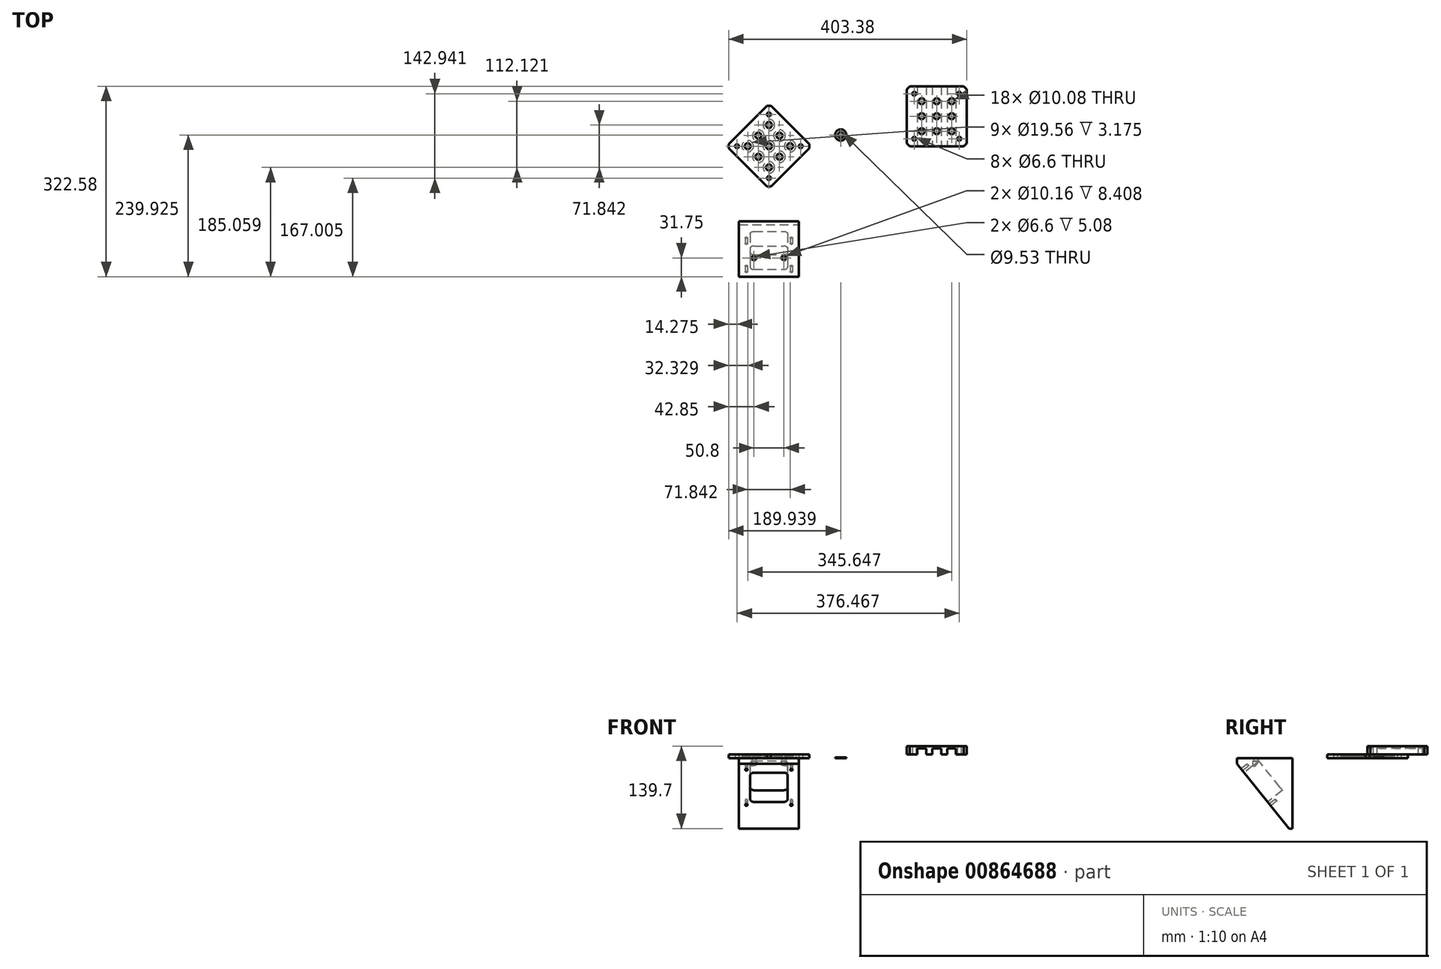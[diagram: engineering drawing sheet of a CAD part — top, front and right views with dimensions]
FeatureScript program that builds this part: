
annotation { "Feature Type Name" : "Feature", "Feature Type Description" : "" }
export const myFeature = defineFeature(function(context is Context, id is Id, definition is map)
    precondition{}
    {
        {
            var Q0;
            Q0=qCreatedBy(makeId("Top.planeOp"),FACE);
            var sketch = newSketch(context, id + "F0", { "sketchPlane" : qUnion([Q0])});
            skCircle(sketch, "E0", {"center": v(0, 0) * mm, "radius": 53.97 * mm, "construction": true});
            skPoint(sketch, "E1", {"position": v(0, 53.97) * mm});
            skPoint(sketch, "E2", {"position": v(53.97, 0) * mm});
            skPoint(sketch, "E3", {"position": v(0, -53.97) * mm});
            skPoint(sketch, "E4", {"position": v(-53.97, 0) * mm});
            skLineSegment(sketch, "E5", {"start": v(0, -71.84) * mm, "end": v(-71.84, 0) * mm});
            skLineSegment(sketch, "E6", {"start": v(-71.84, 0) * mm, "end": v(0, 71.84) * mm});
            skLineSegment(sketch, "E7", {"start": v(0, 71.84) * mm, "end": v(71.84, 0) * mm});
            skLineSegment(sketch, "E8", {"start": v(71.84, 0) * mm, "end": v(0, -71.84) * mm});
            skSolve(sketch);
        }
        {
            var Q0;
            Q0 = qSketchRegion(id + "F0", true);
            extrude(context, id + "F1", {"entities" : qUnion([Q0]), "depth" : 6.35 * mm, "offsetDistance" : 25.4 * mm});
        }
        {
            var Q0;
            Q0=sQuery(id+"F0.wireOp",VERTEX,"E3");
            var Q1;
            Q1=sQuery(id+"F0.wireOp",VERTEX,"E4");
            var Q2;
            Q2=sQuery(id+"F0.wireOp",VERTEX,"E2");
            var Q3;
            Q3=sQuery(id+"F0.wireOp",VERTEX,"E1");
            var Q4;
            Q4=makeQuery(id+"F1.opExtrude","SWEPT_BODY",BODY,{"disambiguationData":[OSD([sQuery(id+"F0.wireOp",EDGE,"E5"),sQuery(id+"F0.wireOp",EDGE,"E6"),sQuery(id+"F0.wireOp",EDGE,"E7"),sQuery(id+"F0.wireOp",EDGE,"E8")])]});
            hole(context, id + "F2", {"style" : HoleStyle.SIMPLE, "endStyle" : HoleEndStyle.THROUGH, "oppositeDirection" : true, "holeDiameter" : 6.6 * mm, "majorDiameter" : 6.35 * mm, "isTappedThrough" : true, "tappedDepth" : 12.7 * mm, "tapClearance" : 3, "locations" : qUnion([Q0, Q1, Q2, Q3]), "scope" : qUnion([Q4])});
        }
        {
            var Q0;
            Q0=makeQuery(id+"F0.imprint","IMPRINT",FACE,{"disambiguationData":[TD([[makeQuery(id+"F0.imprint","IMPRINT",EDGE,{"derivedFrom":sQuery(id+"F0.wireOp",EDGE,"E5")}),-1.0]])]});
            var sketch = newSketch(context, id + "F3", { "sketchPlane" : qUnion([Q0])});
            skPoint(sketch, "E9", {"position": v(0, 0) * mm});
            skPoint(sketch, "E10", {"position": v(-17.96, 17.96) * mm});
            skPoint(sketch, "E11", {"position": v(17.96, -17.96) * mm});
            skPoint(sketch, "E12", {"position": v(-35.92, 0) * mm});
            skPoint(sketch, "E13", {"position": v(-17.96, -17.96) * mm});
            skPoint(sketch, "E14", {"position": v(0, -35.92) * mm});
            skPoint(sketch, "E15", {"position": v(35.92, 0) * mm});
            skPoint(sketch, "E16", {"position": v(17.96, 17.96) * mm});
            skPoint(sketch, "E17", {"position": v(0, 35.92) * mm});
            skLineSegment(sketch, "E18", {"start": v(0, 0) * mm, "end": v(0, -88) * mm});
            skLineSegment(sketch, "E19", {"start": v(0, 0) * mm, "end": v(-58.21, -58.21) * mm});
            skLineSegment(sketch, "E20", {"start": v(-17.96, -17.96) * mm, "end": v(-35.92, 0) * mm});
            skLineSegment(sketch, "E21", {"start": v(-35.92, 0) * mm, "end": v(0, 35.92) * mm});
            skLineSegment(sketch, "E22", {"start": v(0, 35.92) * mm, "end": v(35.92, 0) * mm});
            skLineSegment(sketch, "E23", {"start": v(35.92, 0) * mm, "end": v(0, -35.92) * mm});
            skLineSegment(sketch, "E24", {"start": v(0, -35.92) * mm, "end": v(-17.96, -17.96) * mm});
            skSolve(sketch);
        }
        {
            var Q0;
            Q0=sQuery(id+"F3.wireOp",VERTEX,"E14");
            var Q1;
            Q1=sQuery(id+"F3.wireOp",VERTEX,"E13");
            var Q2;
            Q2=sQuery(id+"F3.wireOp",VERTEX,"E12");
            var Q3;
            Q3=sQuery(id+"F3.wireOp",VERTEX,"E10");
            var Q4;
            Q4=sQuery(id+"F3.wireOp",VERTEX,"E17");
            var Q5;
            Q5=sQuery(id+"F3.wireOp",VERTEX,"E16");
            var Q6;
            Q6=sQuery(id+"F3.wireOp",VERTEX,"E15");
            var Q7;
            Q7=sQuery(id+"F3.wireOp",VERTEX,"E11");
            var Q8;
            Q8=sQuery(id+"F3.wireOp",VERTEX,"E9");
            var Q9;
            Q9=makeQuery(id+"F1.opExtrude","SWEPT_BODY",BODY,{"disambiguationData":[OSD([sQuery(id+"F0.wireOp",EDGE,"E5"),sQuery(id+"F0.wireOp",EDGE,"E6"),sQuery(id+"F0.wireOp",EDGE,"E7"),sQuery(id+"F0.wireOp",EDGE,"E8")])]});
            hole(context, id + "F4", {"style" : HoleStyle.C_BORE, "endStyle" : HoleEndStyle.THROUGH, "oppositeDirection" : true, "holeDiameter" : 10.08 * mm, "cBoreDiameter" : 19.56 * mm, "cBoreDepth" : 3.17 * mm, "majorDiameter" : 6.35 * mm, "isTappedThrough" : true, "tappedDepth" : 12.7 * mm, "tapClearance" : 3, "locations" : qUnion([Q0, Q1, Q2, Q3, Q4, Q5, Q6, Q7, Q8]), "scope" : qUnion([Q9])});
        }
        {
            var Q0;
            Q0=makeQuery(id+"F1.opExtrude","SWEPT_EDGE",EDGE,{"disambiguationData":[OSD([sQuery(id+"F0.wireOp",EDGE,"E5"),sQuery(id+"F0.wireOp",EDGE,"E6")])]});
            var Q1;
            Q1=makeQuery(id+"F1.opExtrude","SWEPT_EDGE",EDGE,{"disambiguationData":[OSD([sQuery(id+"F0.wireOp",EDGE,"E6"),sQuery(id+"F0.wireOp",EDGE,"E7")])]});
            var Q2;
            Q2=makeQuery(id+"F1.opExtrude","SWEPT_EDGE",EDGE,{"disambiguationData":[OSD([sQuery(id+"F0.wireOp",EDGE,"E7"),sQuery(id+"F0.wireOp",EDGE,"E8")])]});
            var Q3;
            Q3=makeQuery(id+"F1.opExtrude","SWEPT_EDGE",EDGE,{"disambiguationData":[OSD([sQuery(id+"F0.wireOp",EDGE,"E5"),sQuery(id+"F0.wireOp",EDGE,"E8")])]});
            chamfer(context, id + "F5", {"entities" : qUnion([Q0, Q1, Q2, Q3]), "width" : 5.08 * mm, "tangentPropagation" : true});
        }
        {
            var Q0;
            Q0=makeQuery(id+"F1.opExtrude","CAP_FACE",FACE,{"disambiguationData":[OSD([sQuery(id+"F0.wireOp",EDGE,"E5"),sQuery(id+"F0.wireOp",EDGE,"E6"),sQuery(id+"F0.wireOp",EDGE,"E7"),sQuery(id+"F0.wireOp",EDGE,"E8")])],"isStart":false});
            var sketch = newSketch(context, id + "F6", { "sketchPlane" : qUnion([Q0])});
            skLineSegment(sketch, "E25.bottom", {"start": v(335.13, 0) * mm, "end": v(233.53, 0) * mm});
            skLineSegment(sketch, "E25.top", {"start": v(335.13, 101.6) * mm, "end": v(233.53, 101.6) * mm});
            skLineSegment(sketch, "E25.left", {"start": v(335.13, 0) * mm, "end": v(335.13, 101.6) * mm});
            skLineSegment(sketch, "E25.right", {"start": v(233.53, 0) * mm, "end": v(233.53, 101.6) * mm});
            skSolve(sketch);
        }
        {
            var Q0;
            Q0 = qSketchRegion(id + "F6", true);
            extrude(context, id + "F7", {"entities" : qUnion([Q0]), "depth" : 13.97 * mm, "offsetDistance" : 25.4 * mm});
        }
        {
            var Q0;
            Q0=makeQuery(id+"F7.opExtrude","CAP_FACE",FACE,{"disambiguationData":[OSD([sQuery(id+"F6.wireOp",EDGE,"E25.bottom"),sQuery(id+"F6.wireOp",EDGE,"E25.top"),sQuery(id+"F6.wireOp",EDGE,"E25.left"),sQuery(id+"F6.wireOp",EDGE,"E25.right")])],"isStart":true});
            var sketch = newSketch(context, id + "F8", { "sketchPlane" : qUnion([Q0])});
            skCircle(sketch, "E26", {"center": v(284.33, -50.8) * mm, "radius": 53.98 * mm});
            skPoint(sketch, "E27", {"position": v(322.5, -88.97) * mm});
            skPoint(sketch, "E28", {"position": v(322.5, -12.63) * mm});
            skPoint(sketch, "E29", {"position": v(246.16, -12.63) * mm});
            skPoint(sketch, "E30", {"position": v(246.16, -88.97) * mm});
            skLineSegment(sketch, "E31", {"start": v(284.33, -50.8) * mm, "end": v(246.16, -88.97) * mm});
            skLineSegment(sketch, "E32", {"start": v(284.33, -50.8) * mm, "end": v(246.16, -12.63) * mm});
            skLineSegment(sketch, "E33", {"start": v(284.33, -50.8) * mm, "end": v(322.5, -12.63) * mm});
            skLineSegment(sketch, "E34", {"start": v(284.33, -50.8) * mm, "end": v(322.5, -88.97) * mm});
            skSolve(sketch);
        }
        {
            var Q0;
            Q0=sQuery(id+"F8.wireOp",VERTEX,"E31.end");
            var Q1;
            Q1=sQuery(id+"F8.wireOp",VERTEX,"E29");
            var Q2;
            Q2=sQuery(id+"F8.wireOp",VERTEX,"E28");
            var Q3;
            Q3=sQuery(id+"F8.wireOp",VERTEX,"E27");
            var Q4;
            Q4=makeQuery(id+"F7.opExtrude","SWEPT_BODY",BODY,{"disambiguationData":[OSD([sQuery(id+"F6.wireOp",EDGE,"E25.bottom"),sQuery(id+"F6.wireOp",EDGE,"E25.top"),sQuery(id+"F6.wireOp",EDGE,"E25.left"),sQuery(id+"F6.wireOp",EDGE,"E25.right")])]});
            hole(context, id + "F9", {"style" : HoleStyle.SIMPLE, "endStyle" : HoleEndStyle.THROUGH, "holeDiameter" : 6.6 * mm, "majorDiameter" : 6.35 * mm, "isTappedThrough" : true, "tappedDepth" : 12.7 * mm, "tapClearance" : 3, "locations" : qUnion([Q0, Q1, Q2, Q3]), "scope" : qUnion([Q4])});
        }
        {
            var Q0;
            Q0=makeQuery(id+"F7.opExtrude","SWEPT_FACE",FACE,{"disambiguationData":[OSD([sQuery(id+"F6.wireOp",EDGE,"E25.bottom")])]});
            var sketch = newSketch(context, id + "F10", { "sketchPlane" : qUnion([Q0])});
            skLineSegment(sketch, "E35.bottom", {"start": v(317.1, 6.35) * mm, "end": v(302.36, 6.35) * mm});
            skLineSegment(sketch, "E35.top", {"start": v(317.1, 16.51) * mm, "end": v(302.36, 16.51) * mm});
            skLineSegment(sketch, "E35.left", {"start": v(317.1, 6.35) * mm, "end": v(317.1, 16.51) * mm});
            skLineSegment(sketch, "E35.right", {"start": v(302.36, 6.35) * mm, "end": v(302.36, 16.5) * mm});
            skLineSegment(sketch, "E36.bottom", {"start": v(291.7, 6.35) * mm, "end": v(276.96, 6.35) * mm});
            skLineSegment(sketch, "E36.top", {"start": v(291.7, 16.51) * mm, "end": v(276.96, 16.51) * mm});
            skLineSegment(sketch, "E36.left", {"start": v(291.7, 6.35) * mm, "end": v(291.7, 16.51) * mm});
            skLineSegment(sketch, "E36.right", {"start": v(276.96, 6.35) * mm, "end": v(276.96, 16.51) * mm});
            skLineSegment(sketch, "E37.bottom", {"start": v(266.3, 6.35) * mm, "end": v(251.56, 6.35) * mm});
            skLineSegment(sketch, "E37.top", {"start": v(266.3, 16.51) * mm, "end": v(251.56, 16.51) * mm});
            skLineSegment(sketch, "E37.left", {"start": v(266.3, 6.35) * mm, "end": v(266.3, 16.51) * mm});
            skLineSegment(sketch, "E37.right", {"start": v(251.56, 6.35) * mm, "end": v(251.56, 16.5) * mm});
            skSolve(sketch);
        }
        {
            var Q0;
            Q0 = qSketchRegion(id + "F10", true);
            extrude(context, id + "F11", {"entities" : qUnion([Q0]), "operationType" : NewBodyOperationType.REMOVE, "endBound" : BoundingType.THROUGH_ALL, "oppositeDirection" : true, "depth" : 25.4 * mm, "offsetDistance" : 25.4 * mm});
        }
        {
            var Q0;
            Q0=makeQuery(id+"F7.opExtrude","SWEPT_EDGE",EDGE,{"disambiguationData":[OSD([sQuery(id+"F6.wireOp",EDGE,"E25.bottom"),sQuery(id+"F6.wireOp",EDGE,"E25.left")])]});
            var Q1;
            Q1=makeQuery(id+"F7.opExtrude","SWEPT_EDGE",EDGE,{"disambiguationData":[OSD([sQuery(id+"F6.wireOp",EDGE,"E25.bottom"),sQuery(id+"F6.wireOp",EDGE,"E25.right")])]});
            var Q2;
            Q2=makeQuery(id+"F7.opExtrude","SWEPT_EDGE",EDGE,{"disambiguationData":[OSD([sQuery(id+"F6.wireOp",EDGE,"E25.top"),sQuery(id+"F6.wireOp",EDGE,"E25.right")])]});
            var Q3;
            Q3=makeQuery(id+"F7.opExtrude","SWEPT_EDGE",EDGE,{"disambiguationData":[OSD([sQuery(id+"F6.wireOp",EDGE,"E25.top"),sQuery(id+"F6.wireOp",EDGE,"E25.left")])]});
            chamfer(context, id + "F12", {"entities" : qUnion([Q0, Q1, Q2, Q3]), "width" : 5.08 * mm, "tangentPropagation" : true});
        }
        {
            var Q0;
            Q0=qCreatedBy(makeId("Top.planeOp"),FACE);
            var sketch = newSketch(context, id + "F13", { "sketchPlane" : qUnion([Q0])});
            skCircle(sketch, "E38", {"center": v(121.69, 18.95) * mm, "radius": 4.76 * mm});
            skCircle(sketch, "E39", {"center": v(121.69, 18.95) * mm, "radius": 9.53 * mm});
            skSolve(sketch);
        }
        {
            var Q0;
            Q0 = qSketchRegion(id + "F13", true);
            extrude(context, id + "F14", {"entities" : qUnion([Q0]), "depth" : 1.02 * mm, "offsetDistance" : 25.4 * mm});
        }
        {
            var Q0;
            Q0=qCreatedBy(makeId("Right.planeOp"),FACE);
            var sketch = newSketch(context, id + "F15", { "sketchPlane" : qUnion([Q0])});
            skLineSegment(sketch, "E40", {"start": v(-228.6, 0) * mm, "end": v(-127, -127) * mm});
            skLineSegment(sketch, "E41", {"start": v(-127, -127) * mm, "end": v(-127, 0) * mm});
            skLineSegment(sketch, "E42", {"start": v(-127, 0) * mm, "end": v(-228.6, 0) * mm});
            skSolve(sketch);
        }
        {
            var Q0;
            Q0 = qSketchRegion(id + "F15", true);
            extrude(context, id + "F16", {"entities" : qUnion([Q0]), "endBound" : BoundingType.SYMMETRIC, "depth" : 101.6 * mm, "offsetDistance" : 25.4 * mm});
        }
        {
            var Q0;
            Q0=makeQuery(id+"F16.opExtrude","SWEPT_FACE",FACE,{"disambiguationData":[OSD([sQuery(id+"F15.wireOp",EDGE,"E40")])]});
            var sketch = newSketch(context, id + "F17", { "sketchPlane" : qUnion([Q0])});
            skCircle(sketch, "E43", {"center": v(0, 79.3) * mm, "radius": 53.98 * mm});
            skLineSegment(sketch, "E44", {"start": v(0, 79.3) * mm, "end": v(-38.17, 41.14) * mm});
            skLineSegment(sketch, "E45", {"start": v(0, 79.3) * mm, "end": v(38.17, 117.47) * mm});
            skLineSegment(sketch, "E46", {"start": v(0, 79.3) * mm, "end": v(38.17, 41.14) * mm});
            skLineSegment(sketch, "E47", {"start": v(0, 79.3) * mm, "end": v(-38.17, 117.47) * mm});
            skLineSegment(sketch, "E48", {"start": v(0, 79.3) * mm, "end": v(0, 25.33) * mm});
            skSolve(sketch);
        }
        {
            var Q0;
            Q0=sQuery(id+"F17.wireOp",VERTEX,"E46.end");
            var Q1;
            Q1=sQuery(id+"F17.wireOp",VERTEX,"E44.end");
            var Q2;
            Q2=sQuery(id+"F17.wireOp",VERTEX,"E47.end");
            var Q3;
            Q3=sQuery(id+"F17.wireOp",VERTEX,"E45.end");
            var Q4;
            Q4=makeQuery(id+"F16.opExtrude","SWEPT_BODY",BODY,{"disambiguationData":[OSD([sQuery(id+"F15.wireOp",EDGE,"E40"),sQuery(id+"F15.wireOp",EDGE,"E41"),sQuery(id+"F15.wireOp",EDGE,"E42")])]});
            hole(context, id + "F18", {"style" : HoleStyle.SIMPLE, "endStyle" : HoleEndStyle.BLIND, "holeDiameter" : 3.97 * mm, "majorDiameter" : 6.35 * mm, "holeDepth" : 12.7 * mm, "isTappedThrough" : true, "tappedDepth" : 12.7 * mm, "tapClearance" : 3, "locations" : qUnion([Q0, Q1, Q2, Q3]), "scope" : qUnion([Q4])});
        }
        {
            var Q0;
            Q0=makeQuery(id+"F16.opExtrude","CAP_FACE",FACE,{"disambiguationData":[OSD([sQuery(id+"F15.wireOp",EDGE,"E40"),sQuery(id+"F15.wireOp",EDGE,"E41"),sQuery(id+"F15.wireOp",EDGE,"E42")])],"isStart":false});
            var sketch = newSketch(context, id + "F19", { "sketchPlane" : qUnion([Q0])});
            skLineSegment(sketch, "E49", {"start": v(-220.98, -9.52) * mm, "end": v(-220.98, 0) * mm});
            skLineSegment(sketch, "E50", {"start": v(-220.98, 0) * mm, "end": v(-228.6, 0) * mm});
            skLineSegment(sketch, "E51", {"start": v(-228.6, 0) * mm, "end": v(-220.98, -9.52) * mm});
            skLineSegment(sketch, "E52", {"start": v(-127, -127) * mm, "end": v(-127, -119.38) * mm});
            skLineSegment(sketch, "E53", {"start": v(-127, -119.38) * mm, "end": v(-133.1, -119.38) * mm});
            skLineSegment(sketch, "E54", {"start": v(-133.1, -119.38) * mm, "end": v(-127, -127) * mm});
            skSolve(sketch);
        }
        {
            var Q0;
            Q0=makeQuery(id+"F19.imprint","IMPRINT",FACE,{"disambiguationData":[TD([[makeQuery(id+"F19.imprint","IMPRINT",EDGE,{"derivedFrom":sQuery(id+"F19.wireOp",EDGE,"E49")}),1.0]])]});
            var Q1;
            Q1=makeQuery(id+"F19.imprint","IMPRINT",FACE,{"disambiguationData":[TD([[makeQuery(id+"F19.imprint","IMPRINT",EDGE,{"derivedFrom":sQuery(id+"F19.wireOp",EDGE,"E52")}),1.0]])]});
            extrude(context, id + "F20", {"entities" : qUnion([Q0, Q1]), "operationType" : NewBodyOperationType.REMOVE, "endBound" : BoundingType.THROUGH_ALL, "oppositeDirection" : true, "depth" : 25.4 * mm, "offsetDistance" : 25.4 * mm});
        }
        {
            var Q0;
            Q0=makeQuery(id+"F20.boolean.opBoolean","COPY",FACE,{"derivedFrom":makeQuery(id+"F20.opExtrude","SWEPT_FACE",FACE,{"disambiguationData":[OSD([sQuery(id+"F19.wireOp",EDGE,"E53")])]})});
            var sketch = newSketch(context, id + "F21", { "sketchPlane" : qUnion([Q0])});
            skPoint(sketch, "E55", {"position": v(-25.4, 189.23) * mm});
            skPoint(sketch, "E56", {"position": v(25.4, 189.23) * mm});
            skSolve(sketch);
        }
        {
            var Q0;
            Q0=sQuery(id+"F21.wireOp",VERTEX,"E55");
            var Q1;
            Q1=sQuery(id+"F21.wireOp",VERTEX,"E56");
            var Q2;
            Q2=makeQuery(id+"F16.opExtrude","SWEPT_BODY",BODY,{"disambiguationData":[OSD([sQuery(id+"F15.wireOp",EDGE,"E40"),sQuery(id+"F15.wireOp",EDGE,"E41"),sQuery(id+"F15.wireOp",EDGE,"E42")])]});
            hole(context, id + "F22", {"style" : HoleStyle.C_BORE, "endStyle" : HoleEndStyle.THROUGH, "holeDiameter" : 6.6 * mm, "cBoreDiameter" : 10.16 * mm, "cBoreDepth" : 114.3 * mm, "majorDiameter" : 6.35 * mm, "isTappedThrough" : true, "tappedDepth" : 12.7 * mm, "tapClearance" : 3, "startFromSketch" : true, "locations" : qUnion([Q0, Q1]), "scope" : qUnion([Q2])});
        }
        {
            var Q0;
            Q0=makeQuery(id+"F16.opExtrude","SWEPT_FACE",FACE,{"disambiguationData":[OSD([sQuery(id+"F15.wireOp",EDGE,"E40")])]});
            var sketch = newSketch(context, id + "F23", { "sketchPlane" : qUnion([Q0])});
            skLineSegment(sketch, "E57.bottom", {"start": v(-31.75, 47.56) * mm, "end": v(31.75, 47.56) * mm});
            skLineSegment(sketch, "E57.top", {"start": v(-31.75, 111.06) * mm, "end": v(31.75, 111.06) * mm});
            skLineSegment(sketch, "E57.left", {"start": v(-31.75, 47.56) * mm, "end": v(-31.75, 111.06) * mm});
            skLineSegment(sketch, "E57.right", {"start": v(31.75, 47.56) * mm, "end": v(31.75, 111.06) * mm});
            skPoint(sketch, "E57.middle", {"position": v(0, 79.3) * mm});
            skLineSegment(sketch, "E58", {"start": v(38.17, 117.47) * mm, "end": v(-38.17, 41.14) * mm, "construction": true});
            skSolve(sketch);
        }
        {
            var Q0;
            Q0 = qSketchRegion(id + "F23", true);
            extrude(context, id + "F24", {"entities" : qUnion([Q0]), "operationType" : NewBodyOperationType.REMOVE, "oppositeDirection" : true, "depth" : 31.75 * mm, "offsetDistance" : 25.4 * mm});
        }
        {
            var Q0;
            Q0=makeQuery(id+"F11.boolean.opBoolean","COPY",FACE,{"derivedFrom":makeQuery(id+"F11.opExtrude","SWEPT_FACE",FACE,{"disambiguationData":[OSD([sQuery(id+"F10.wireOp",EDGE,"E36.top")])]})});
            var sketch = newSketch(context, id + "F25", { "sketchPlane" : qUnion([Q0])});
            skPoint(sketch, "E59", {"position": v(284.33, -50.8) * mm});
            skPoint(sketch, "E60", {"position": v(284.33, -25.4) * mm});
            skPoint(sketch, "E61", {"position": v(284.33, -76.2) * mm});
            skPoint(sketch, "E62", {"position": v(258.93, -76.2) * mm});
            skPoint(sketch, "E63", {"position": v(258.93, -50.8) * mm});
            skPoint(sketch, "E64", {"position": v(258.93, -25.4) * mm});
            skPoint(sketch, "E65", {"position": v(309.73, -25.4) * mm});
            skPoint(sketch, "E66", {"position": v(309.73, -50.8) * mm});
            skPoint(sketch, "E67", {"position": v(309.73, -76.2) * mm});
            skSolve(sketch);
        }
        {
            var Q0;
            Q0=sQuery(id+"F25.wireOp",VERTEX,"E64");
            var Q1;
            Q1=sQuery(id+"F25.wireOp",VERTEX,"E63");
            var Q2;
            Q2=sQuery(id+"F25.wireOp",VERTEX,"E62");
            var Q3;
            Q3=sQuery(id+"F25.wireOp",VERTEX,"E61");
            var Q4;
            Q4=sQuery(id+"F25.wireOp",VERTEX,"E59");
            var Q5;
            Q5=sQuery(id+"F25.wireOp",VERTEX,"E60");
            var Q6;
            Q6=sQuery(id+"F25.wireOp",VERTEX,"E65");
            var Q7;
            Q7=sQuery(id+"F25.wireOp",VERTEX,"E66");
            var Q8;
            Q8=sQuery(id+"F25.wireOp",VERTEX,"E67");
            var Q9;
            Q9=makeQuery(id+"F7.opExtrude","SWEPT_BODY",BODY,{"disambiguationData":[OSD([sQuery(id+"F6.wireOp",EDGE,"E25.bottom"),sQuery(id+"F6.wireOp",EDGE,"E25.top"),sQuery(id+"F6.wireOp",EDGE,"E25.left"),sQuery(id+"F6.wireOp",EDGE,"E25.right")])]});
            hole(context, id + "F26", {"style" : HoleStyle.SIMPLE, "endStyle" : HoleEndStyle.BLIND, "holeDiameter" : 10.08 * mm, "majorDiameter" : 6.35 * mm, "holeDepth" : 25.4 * mm, "tappedDepth" : 10.3 * mm, "tapClearance" : 3, "startFromSketch" : true, "locations" : qUnion([Q0, Q1, Q2, Q3, Q4, Q5, Q6, Q7, Q8]), "scope" : qUnion([Q9])});
        }
        {
            var Q0;
            Q0=makeQuery(id+"F24.boolean.opBoolean","COPY",EDGE,{"derivedFrom":makeQuery(id+"F24.opExtrude","SWEPT_EDGE",EDGE,{"disambiguationData":[OSD([sQuery(id+"F23.wireOp",EDGE,"E57.top"),sQuery(id+"F23.wireOp",EDGE,"E57.left")])]})});
            var Q1;
            Q1=makeQuery(id+"F24.boolean.opBoolean","COPY",EDGE,{"derivedFrom":makeQuery(id+"F24.opExtrude","SWEPT_EDGE",EDGE,{"disambiguationData":[OSD([sQuery(id+"F23.wireOp",EDGE,"E57.bottom"),sQuery(id+"F23.wireOp",EDGE,"E57.left")])]})});
            var Q2;
            Q2=makeQuery(id+"F24.boolean.opBoolean","COPY",EDGE,{"derivedFrom":makeQuery(id+"F24.opExtrude","SWEPT_EDGE",EDGE,{"disambiguationData":[OSD([sQuery(id+"F23.wireOp",EDGE,"E57.bottom"),sQuery(id+"F23.wireOp",EDGE,"E57.right")])]})});
            var Q3;
            Q3=makeQuery(id+"F24.boolean.opBoolean","COPY",EDGE,{"derivedFrom":makeQuery(id+"F24.opExtrude","SWEPT_EDGE",EDGE,{"disambiguationData":[OSD([sQuery(id+"F23.wireOp",EDGE,"E57.top"),sQuery(id+"F23.wireOp",EDGE,"E57.right")])]})});
            fillet(context, id + "F27", {"entities" : qUnion([Q0, Q1, Q2, Q3]), "radius" : 6.35 * mm, "tangentPropagation" : true, "allowEdgeOverflow" : false});
        }
    });
